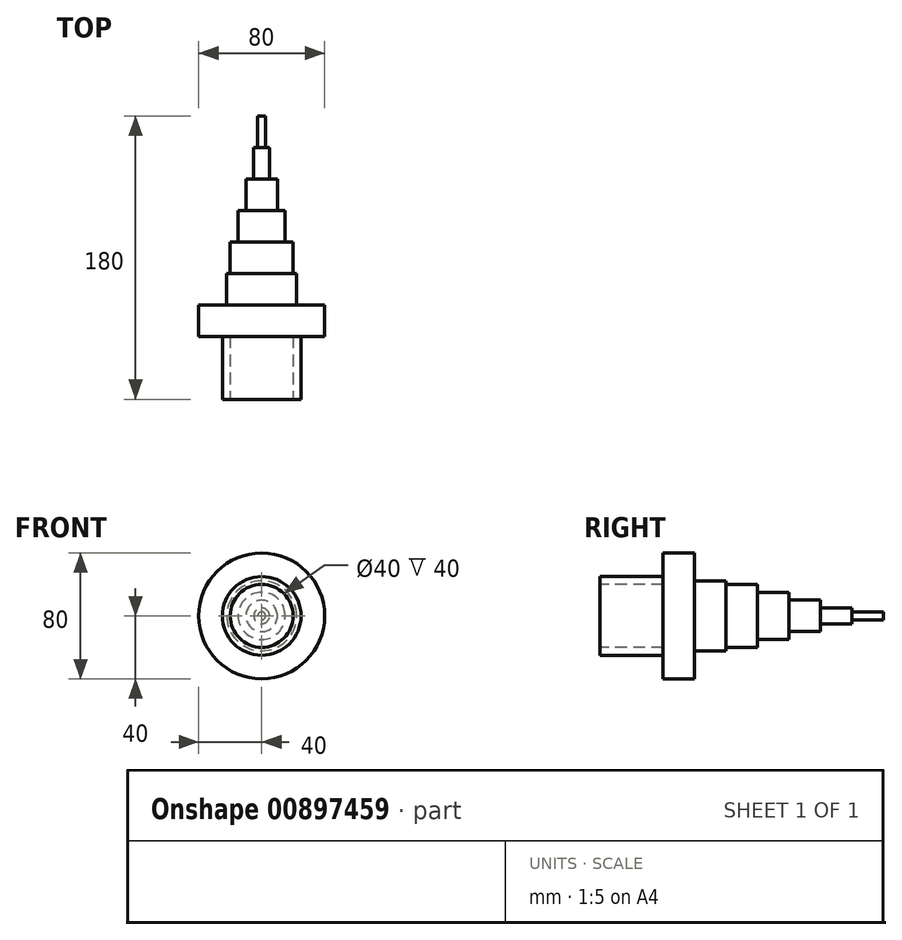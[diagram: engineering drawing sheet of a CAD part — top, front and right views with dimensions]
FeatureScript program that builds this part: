
annotation { "Feature Type Name" : "Feature", "Feature Type Description" : "" }
export const myFeature = defineFeature(function(context is Context, id is Id, definition is map)
    precondition{}
    {
        {
            var Q0;
            Q0=qCreatedBy(makeId("Front.planeOp"),FACE);
            var sketch = newSketch(context, id + "F0", { "sketchPlane" : qUnion([Q0])});
            skCircle(sketch, "E0", {"center": v(0, 0) * mm, "radius": 40 * mm});
            skSolve(sketch);
        }
        {
            var Q0;
            Q0 = qSketchRegion(id + "F0", true);
            extrude(context, id + "F1", {"entities" : qUnion([Q0]), "depth" : 20 * mm, "offsetDistance" : 25.4 * mm});
        }
        {
            var Q0;
            Q0=makeQuery(id+"F1.opExtrude","CAP_FACE",FACE,{"disambiguationData":[OSD([sQuery(id+"F0.wireOp",EDGE,"E0")])],"isStart":false});
            var sketch = newSketch(context, id + "F2", { "sketchPlane" : qUnion([Q0])});
            skCircle(sketch, "E1", {"center": v(0, 0) * mm, "radius": 25 * mm});
            skSolve(sketch);
        }
        {
            var Q0;
            Q0=makeQuery(id+"F2.imprint","IMPRINT",FACE,{"disambiguationData":[TD([[makeQuery(id+"F2.imprint","IMPRINT",EDGE,{"derivedFrom":sQuery(id+"F2.wireOp",EDGE,"E1")}),1.0]])]});
            extrude(context, id + "F3", {"entities" : qUnion([Q0]), "operationType" : NewBodyOperationType.ADD, "depth" : 40 * mm, "offsetDistance" : 25.4 * mm});
        }
        {
            var Q0;
            Q0=makeQuery(id+"F3.opExtrude","CAP_FACE",FACE,{"disambiguationData":[OSD([sQuery(id+"F2.wireOp",EDGE,"E1")])],"isStart":false});
            var sketch = newSketch(context, id + "F4", { "sketchPlane" : qUnion([Q0])});
            skCircle(sketch, "E2", {"center": v(0, 0) * mm, "radius": 20 * mm});
            skSolve(sketch);
        }
        {
            var Q0;
            Q0 = qSketchRegion(id + "F4", true);
            extrude(context, id + "F5", {"entities" : qUnion([Q0]), "operationType" : NewBodyOperationType.REMOVE, "oppositeDirection" : true, "depth" : 40 * mm, "offsetDistance" : 25.4 * mm});
        }
        {
            var Q0;
            Q0=makeQuery(id+"F1.opExtrude","CAP_FACE",FACE,{"disambiguationData":[OSD([sQuery(id+"F0.wireOp",EDGE,"E0")])],"isStart":true});
            var sketch = newSketch(context, id + "F6", { "sketchPlane" : qUnion([Q0])});
            skCircle(sketch, "E3", {"center": v(0, 0) * mm, "radius": 22.2 * mm});
            skSolve(sketch);
        }
        {
            var Q0;
            Q0=makeQuery(id+"F6.imprint","IMPRINT",FACE,{"disambiguationData":[TD([[makeQuery(id+"F6.imprint","IMPRINT",EDGE,{"derivedFrom":sQuery(id+"F6.wireOp",EDGE,"E3")}),1.0]])]});
            extrude(context, id + "F7", {"entities" : qUnion([Q0]), "operationType" : NewBodyOperationType.ADD, "depth" : 20 * mm, "offsetDistance" : 25.4 * mm});
        }
        {
            var Q0;
            Q0=makeQuery(id+"F7.opExtrude","CAP_FACE",FACE,{"disambiguationData":[OSD([sQuery(id+"F6.wireOp",EDGE,"E3")])],"isStart":false});
            var sketch = newSketch(context, id + "F8", { "sketchPlane" : qUnion([Q0])});
            skCircle(sketch, "E4", {"center": v(0, 0) * mm, "radius": 20 * mm});
            skSolve(sketch);
        }
        {
            var Q0;
            Q0=makeQuery(id+"F8.imprint","IMPRINT",FACE,{"disambiguationData":[TD([[makeQuery(id+"F8.imprint","IMPRINT",EDGE,{"derivedFrom":sQuery(id+"F8.wireOp",EDGE,"E4")}),1.0]])]});
            extrude(context, id + "F9", {"entities" : qUnion([Q0]), "operationType" : NewBodyOperationType.ADD, "depth" : 20 * mm, "offsetDistance" : 25.4 * mm});
        }
        {
            var Q0;
            Q0=makeQuery(id+"F9.opExtrude","CAP_FACE",FACE,{"disambiguationData":[OSD([sQuery(id+"F8.wireOp",EDGE,"E4")])],"isStart":false});
            var sketch = newSketch(context, id + "F10", { "sketchPlane" : qUnion([Q0])});
            skCircle(sketch, "E5", {"center": v(0, 0) * mm, "radius": 15 * mm});
            skSolve(sketch);
        }
        {
            var Q0;
            Q0=makeQuery(id+"F10.imprint","IMPRINT",FACE,{"disambiguationData":[TD([[makeQuery(id+"F10.imprint","IMPRINT",EDGE,{"derivedFrom":sQuery(id+"F10.wireOp",EDGE,"E5")}),1.0]])]});
            extrude(context, id + "F11", {"entities" : qUnion([Q0]), "operationType" : NewBodyOperationType.ADD, "depth" : 20 * mm, "offsetDistance" : 25.4 * mm});
        }
        {
            var Q0;
            Q0=makeQuery(id+"F11.opExtrude","CAP_FACE",FACE,{"disambiguationData":[OSD([sQuery(id+"F10.wireOp",EDGE,"E5")])],"isStart":false});
            var sketch = newSketch(context, id + "F12", { "sketchPlane" : qUnion([Q0])});
            skCircle(sketch, "E6", {"center": v(0, 0) * mm, "radius": 10 * mm});
            skSolve(sketch);
        }
        {
            var Q0;
            Q0 = qSketchRegion(id + "F12", true);
            extrude(context, id + "F13", {"entities" : qUnion([Q0]), "operationType" : NewBodyOperationType.ADD, "depth" : 20 * mm, "offsetDistance" : 25.4 * mm});
        }
        {
            var Q0;
            Q0=makeQuery(id+"F13.opExtrude","CAP_FACE",FACE,{"disambiguationData":[OSD([sQuery(id+"F12.wireOp",EDGE,"E6")])],"isStart":false});
            var sketch = newSketch(context, id + "F14", { "sketchPlane" : qUnion([Q0])});
            skCircle(sketch, "E7", {"center": v(0, 0) * mm, "radius": 5 * mm});
            skSolve(sketch);
        }
        {
            var Q0;
            Q0 = qSketchRegion(id + "F14", true);
            extrude(context, id + "F15", {"entities" : qUnion([Q0]), "operationType" : NewBodyOperationType.ADD, "depth" : 20 * mm, "offsetDistance" : 25.4 * mm});
        }
        {
            var Q0;
            Q0=makeQuery(id+"F15.opExtrude","CAP_FACE",FACE,{"disambiguationData":[OSD([sQuery(id+"F14.wireOp",EDGE,"E7")])],"isStart":false});
            var sketch = newSketch(context, id + "F16", { "sketchPlane" : qUnion([Q0])});
            skCircle(sketch, "E8", {"center": v(0, 0) * mm, "radius": 2.5 * mm});
            skSolve(sketch);
        }
        {
            var Q0;
            Q0 = qSketchRegion(id + "F16", true);
            extrude(context, id + "F17", {"entities" : qUnion([Q0]), "operationType" : NewBodyOperationType.ADD, "depth" : 20 * mm, "offsetDistance" : 25.4 * mm});
        }
    });
